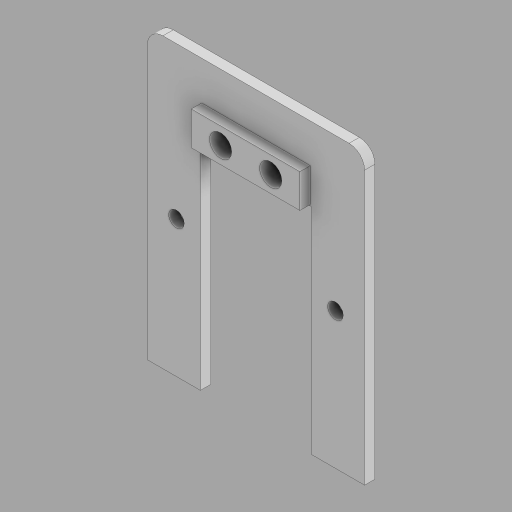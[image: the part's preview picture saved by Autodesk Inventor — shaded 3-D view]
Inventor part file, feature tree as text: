
AUTODESK INVENTOR PART (.ipt)
format: ipt  version: 2023.2 (Build 272271030, 271C)  size: 502,272 bytes
history: native  units: mm
features: sketch x7, extrude x7, projected_geometry x5, fillet x1
ambient origin geometry x8: Origin, YZ Plane, XZ Plane, XY Plane, X Axis, Y Axis, Z Axis, Center Point
bodies: Solid1 (feature_tree)
feature tree (20):
  sketch  "Sketch1"  dims[d0=42.0mm d1=70.0mm d4=21.5mm]
  extrude  "Extrusion1"  Depth=70.0mm
  fillet  "Fillet3"  Radius=21.5mm
  extrude  "Extrusion11"  Depth=2.0mm TaperAngle=0.0deg
  extrude  "Extrusion12"  Depth=3.0mm
  extrude  "Extrusion15"  Depth=4.3mm
  extrude  "Extrusion16"  Depth=9.7mm
  sketch  "Sketch22"  dims[d55=4.3mm d56=9.7mm]
  extrude  "Extrusion20"  Depth=7.0mm
  extrude  "Extrusion21"  Depth=10.0mm
  sketch  "Sketch14"  dims[d5=41.5mm d6=2.0mm d7=0.0mm]
  projected_geometry  "Projected Loop9"
  sketch  "Sketch17"  dims[d18=3.85mm d38=3.0mm]
  projected_geometry  "Projected Loop12"
  sketch  "Sketch18"  dims[d52=6.0mm d53=0.0mm d54=4.3mm]
  projected_geometry  "Projected Loop13"
  sketch  "Sketch23"  dims[d59=6.0mm d60=0.0mm d67=7.0mm]
  projected_geometry  "Projected Loop15"
  sketch  "Sketch24"  dims[d68=2.0mm d69=0.0mm d70=4.625mm d71=28.375mm d72=3.0mm d73=10.0mm d74=0.0mm d75=30.75mm d88=0.25mm d89=2.0mm d90=0.0mm d91=10.0mm d92=0.0mm d39=0.5mm d40=0.872665mm d41=0.5mm d42=0.872665mm]
  projected_geometry  "Projected Loop16"
